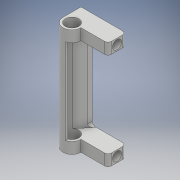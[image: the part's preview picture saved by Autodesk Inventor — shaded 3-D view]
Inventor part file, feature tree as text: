
AUTODESK INVENTOR PART (.ipt)
format: ipt  version: 2018.3 (Build 223284000, 284)  size: 159,744 bytes
history: native  units: mm
features: extrude x3, sketch x3, projected_geometry x3, fillet x2, chamfer x1
ambient origin geometry x8: Origin, YZ Plane, XZ Plane, XY Plane, X Axis, Y Axis, Z Axis, Center Point
bodies: Solid1 (feature_tree)
feature tree (12):
  extrude  "Extrusion1"  Depth=2.0mm
  extrude  "Extrusion2"  Depth=10.0mm
  extrude  "Extrusion3"  Depth=8.0mm
  chamfer  "Chamfer1"  Distance=8.0mm
  fillet  "Fillet1"  Radius=15.0mm
  fillet  "Fillet2"  Radius=6.0mm
  sketch  "Sketch1"  dims[d0=12.0mm d1=2.0mm]
  sketch  "Sketch2"  dims[d3=95.9mm d4=0.0mm d5=10.0mm]
  projected_geometry  "Projected Loop1"
  sketch  "Sketch3"  dims[d6=95.9mm d7=0.0mm d9=8.0mm d10=8.0mm d11=15.0mm d12=0.0mm d13=6.0mm d14=2.0mm d15=45.0deg d16=3.0mm d17=3.0mm]
  projected_geometry  "Projected Loop2"
  projected_geometry  "Projected Loop3"
